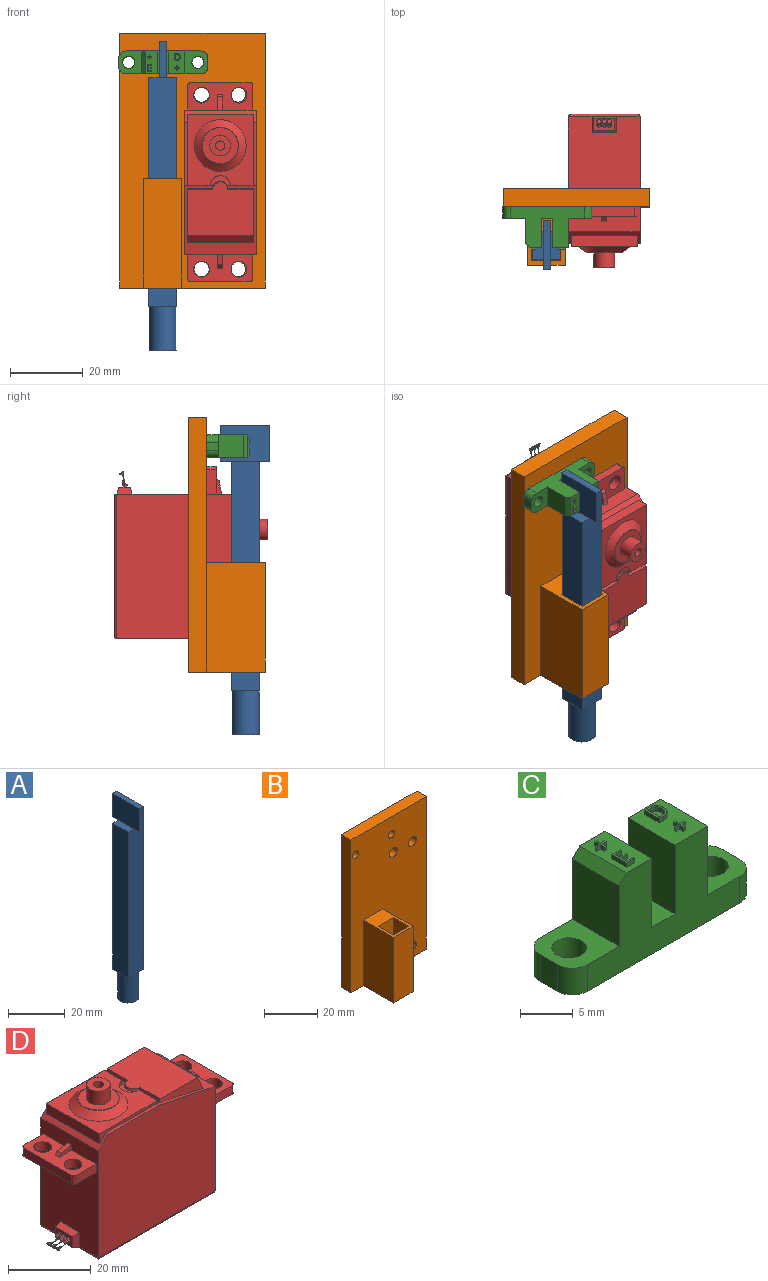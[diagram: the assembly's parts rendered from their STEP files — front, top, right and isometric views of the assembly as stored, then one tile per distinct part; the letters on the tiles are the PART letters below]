
ASSEMBLY  parts=4 mates=4
PART A: 16 faces, bbox 7.7x13.5x85 mm
  f0: plane 63x7.7mm, normal (0,1,0), area 485.1mm2, adj f1,f3,f4,f5,f12,f13
  f1: plane 63x7.7mm, normal (-1,0,0), area 485.1mm2, adj f0,f2,f5,f13
  f2: plane 63x7.7mm, normal (0,-1,0), area 485.1mm2, adj f1,f3,f4,f5,f6,f13
  f3: plane 63x7.7mm, normal (1,0,0), area 485.1mm2, adj f0,f2,f4,f13
  f4: plane 7.7x2.85mm, normal (0,0,1), area 21.9mm2, adj f0,f2,f3,f10
  f5: plane 7.7x2.85mm, normal (0,0,1), area 21.9mm2, adj f0,f1,f2,f8
  f6: plane 2.81x2mm, normal (0,0,-1), area 5.6mm2, adj f2,f8,f9,f10
  f7: plane 10x2mm, normal (0,1,0), area 20mm2, adj f8,f10,f11,f12
  f8: plane 13.51x10mm, normal (-1,0,0), area 135.1mm2, adj f5,f6,f7,f9,f11,f12
  f9: plane 10x2mm, normal (0,-1,0), area 20mm2, adj f6,f8,f10,f11
  f10: plane 13.51x10mm, normal (1,0,0), area 135.1mm2, adj f4,f6,f7,f9,f11,f12
  f11: plane 13.51x2mm, normal (0,0,1), area 27mm2, adj f7,f8,f9,f10
  f12: plane 3x2mm, normal (0,0,-1), area 6mm2, adj f0,f7,f8,f10
  f13: plane 7.7x7.7mm, normal (0,0,-1), area 15.1mm2, adj f0,f1,f2,f3,f14
  f14: cylinder r=3.75mm len=12mm, axis (0,0,-1), area 282.7mm2, adj f13,f15
  f15: plane 7.5x7.5mm, normal (0,0,-1), area 44.2mm2, adj f14
PART B: 20 faces, bbox 40x21x70 mm
  f0: plane 40x5mm, normal (0,0,1), area 200mm2, adj f1,f3,f4,f5
  f1: plane 70x5mm, normal (-1,0,0), area 350mm2, adj f0,f2,f4,f5
  f2: plane 40x21mm, normal (0,0,-1), area 302.4mm2, adj f1,f3,f4,f5,f6,f7,f8,f9
  f3: plane 70x5mm, normal (1,0,0), area 350mm2, adj f0,f2,f4,f5
  f4: plane 70x40mm, normal (0,-1,0), area 2415.5mm2, adj f0,f1,f2,f3,f6,f12,f13,f14
  f5: plane 70x40mm, normal (0,1,0), area 2727.5mm2, adj f0,f1,f2,f3,f14,f15,f16,f17
  f6: plane 30x16mm, normal (-1,0,0), area 480mm2, adj f2,f4,f7,f13
  f7: plane 30x10.4mm, normal (0,-1,0), area 312mm2, adj f2,f6,f12,f13
  f8: plane 30x8mm, normal (1,0,0), area 240mm2, adj f2,f9,f11,f13
  f9: plane 30x8mm, normal (0,-1,0), area 240mm2, adj f2,f8,f10,f13
  f10: plane 30x8mm, normal (-1,0,0), area 240mm2, adj f2,f9,f11,f13
  f11: plane 30x8mm, normal (0,1,0), area 240mm2, adj f2,f8,f10,f13
  f12: plane 30x16mm, normal (1,0,0), area 480mm2, adj f2,f4,f7,f13
  f13: plane 16x10.4mm, normal (0,0,1), area 102.4mm2, adj f4,f6,f7,f8,f9,f10,f11,f12
  f14: cylinder r=2.1mm len=5mm, axis (0,-1,0), area 66mm2, adj f4,f5
  f15: cylinder r=2.1mm len=5mm, axis (0,-1,0), area 66mm2, adj f4,f5
  f16: cylinder r=2.1mm len=5mm, axis (0,-1,0), area 66mm2, adj f4,f5
  f17: cylinder r=2.1mm len=5mm, axis (0,-1,0), area 66mm2, adj f4,f5
  f18: cylinder r=1.65mm len=5mm, axis (0,-1,0), area 51.8mm2, adj f4,f5
  f19: cylinder r=1.65mm len=5mm, axis (0,-1,0), area 51.8mm2, adj f4,f5
PART C: 76 faces, bbox 24.5x6.3x11.6 mm
  f0: plane 6.3x4.4mm, normal (0,0,1), area 24.5mm2, adj f2,f3,f9,f11,f53,f54,f55,f56
  f1: plane 6.3x3.4mm, normal (0,0,1), area 20mm2, adj f2,f3,f7,f14,f21,f22,f23,f24
  f2: plane 20.5x11.1mm, normal (0,1,0), area 133.5mm2, adj f0,f1,f6,f7,f8,f9,f10,f11
  f3: plane 20.5x11.1mm, normal (0,-1,0), area 133.5mm2, adj f0,f1,f6,f7,f8,f9,f10,f11
  f4: plane 3.1x2.3mm, normal (-1,0,0), area 7.1mm2, adj f6,f12,f17,f18
  f5: plane 3.1x2.3mm, normal (1,0,0), area 7.1mm2, adj f6,f10,f19,f20
  f6: plane 24.5x6.3mm, normal (0,0,-1), area 133.8mm2, adj f2,f3,f4,f5,f15,f16,f17,f18
  f7: plane 8x6.3mm, normal (1,0,0), area 50.4mm2, adj f1,f2,f3,f8
  f8: plane 6.3x3.1mm, normal (0,0,1), area 19.5mm2, adj f2,f3,f7,f9
  f9: plane 8x6.3mm, normal (-1,0,0), area 50.4mm2, adj f0,f2,f3,f8
  f10: plane 6.3x6.3mm, normal (0,0,1), area 29.4mm2, adj f2,f3,f5,f11,f16,f19,f20
  f11: plane 8x6.3mm, normal (1,0,0), area 50.4mm2, adj f0,f2,f3,f10
  f12: plane 6.3x6.3mm, normal (0,0,1), area 29.4mm2, adj f2,f3,f4,f13,f15,f17,f18
  f13: plane 7x6.3mm, normal (-1,0,0), area 44.1mm2, adj f2,f3,f12,f14
  f14: plane 6.3x1mm, normal (-0.71,0,0.71), area 8.9mm2, adj f1,f2,f3,f13
  f15: cylinder r=1.65mm len=3.3mm, axis (0,0,-1), area 32.1mm2, adj f6,f12
  f16: cylinder r=1.65mm len=3.3mm, axis (0,0,-1), area 32.1mm2, adj f6,f10
  f17: cylinder r=2mm len=3.1mm, axis (0,0,1), area 9.7mm2, adj f2,f4,f6,f12
  f18: cylinder r=2mm len=3.1mm, axis (0,0,-1), area 9.7mm2, adj f3,f4,f6,f12
  f19: cylinder r=2mm len=3.1mm, axis (0,0,1), area 9.7mm2, adj f3,f5,f6,f10
  f20: cylinder r=2mm len=3.1mm, axis (0,0,-1), area 9.7mm2, adj f2,f5,f6,f10
  f21: plane 0.56x0.5mm, normal (0,1,0), area 0.3mm2, adj f1,f22,f32,f33
  f22: plane 0.58x0.5mm, normal (1,0,0), area 0.3mm2, adj f1,f21,f23,f33
  f23: plane 0.5x0.19mm, normal (0,1,0), area 0.1mm2, adj f1,f22,f24,f33
  f24: plane 0.58x0.5mm, normal (-1,0,0), area 0.3mm2, adj f1,f23,f25,f33
  f25: plane 0.56x0.5mm, normal (0,1,0), area 0.3mm2, adj f1,f24,f26,f33
  f26: plane 0.5x0.19mm, normal (-1,0,0), area 0.1mm2, adj f1,f25,f27,f33
  f27: plane 0.56x0.5mm, normal (0,-1,0), area 0.3mm2, adj f1,f26,f28,f33
  f28: plane 0.58x0.5mm, normal (-1,0,0), area 0.3mm2, adj f1,f27,f29,f33
  f29: plane 0.5x0.19mm, normal (0,-1,0), area 0.1mm2, adj f1,f28,f30,f33
  f30: plane 0.58x0.5mm, normal (1,0,0), area 0.3mm2, adj f1,f29,f31,f33
  f31: plane 0.56x0.5mm, normal (0,-1,0), area 0.3mm2, adj f1,f30,f32,f33
  f32: plane 0.5x0.19mm, normal (1,0,0), area 0.1mm2, adj f1,f21,f31,f33
  f33: plane 1.35x1.3mm, normal (0,0,1), area 0.5mm2, adj f21,f22,f23,f24,f25,f26,f27,f28
  f34: plane 1.11x0.5mm, normal (0,-1,0), area 0.6mm2, adj f1,f35,f45,f46
  f35: plane 0.5x0.21mm, normal (1,0,0), area 0.1mm2, adj f1,f34,f36,f46
  f36: plane 0.88x0.5mm, normal (0,1,0), area 0.4mm2, adj f1,f35,f37,f46
  f37: plane 0.73x0.5mm, normal (1,0,0), area 0.4mm2, adj f1,f36,f38,f46
  f38: plane 0.82x0.5mm, normal (0,-1,0), area 0.4mm2, adj f1,f37,f39,f46
  f39: plane 0.5x0.2mm, normal (1,0,0), area 0.1mm2, adj f1,f38,f40,f46
  f40: plane 0.82x0.5mm, normal (0,1,0), area 0.4mm2, adj f1,f39,f41,f46
  f41: plane 0.64x0.5mm, normal (1,0,0), area 0.3mm2, adj f1,f40,f42,f46
  f42: plane 0.88x0.5mm, normal (0,-1,0), area 0.4mm2, adj f1,f41,f43,f46
  f43: plane 0.5x0.21mm, normal (1,0,0), area 0.1mm2, adj f1,f42,f44,f46
  f44: plane 1.11x0.5mm, normal (0,1,0), area 0.6mm2, adj f1,f43,f45,f46
  f45: plane 1.98x0.5mm, normal (-1,0,0), area 1mm2, adj f1,f34,f44,f46
  f46: plane 1.98x1.11mm, normal (0,0,1), area 1mm2, adj f34,f35,f36,f37,f38,f39,f40,f41
  f47: extruded ~0.58x0.5mm, area 0.3mm2, adj f48,f60,f61,f62
  f48: extruded ~0.6x0.5mm, area 0.3mm2, adj f47,f49,f61,f62
  f49: extruded ~0.62x0.5mm, area 0.3mm2, adj f48,f50,f61,f62
  f50: plane 0.5x0.28mm, normal (0,1,0), area 0.1mm2, adj f49,f51,f61,f62
  f51: plane 1.58x0.5mm, normal (1,0,0), area 0.8mm2, adj f50,f52,f61,f62
  f52: plane 0.5x0.34mm, normal (0,-1,0), area 0.2mm2, adj f51,f60,f61,f62
  f53: extruded ~0.75x0.5mm, area 0.4mm2, adj f0,f54,f59,f61
  f54: extruded ~0.72x0.5mm, area 0.4mm2, adj f0,f53,f55,f61
  f55: extruded ~0.72x0.5mm, area 0.4mm2, adj f0,f54,f56,f61
  f56: plane 0.61x0.5mm, normal (0,1,0), area 0.3mm2, adj f0,f55,f57,f61
  f57: plane 1.98x0.5mm, normal (-1,0,0), area 1mm2, adj f0,f56,f58,f61
  f58: plane 0.55x0.5mm, normal (0,-1,0), area 0.3mm2, adj f0,f57,f59,f61
  f59: extruded ~0.77x0.5mm, area 0.4mm2, adj f0,f53,f58,f61
  f60: extruded ~0.58x0.5mm, area 0.3mm2, adj f47,f52,f61,f62
  f61: plane 1.98x1.58mm, normal (0,0,1), area 1.2mm2, adj f47,f48,f49,f50,f51,f52,f53,f54
  f62: plane 1.58x1.11mm, normal (0,0,1), area 1.5mm2, adj f47,f48,f49,f50,f51,f52,f60
  f63: plane 0.56x0.5mm, normal (0,1,0), area 0.3mm2, adj f0,f64,f74,f75
  f64: plane 0.58x0.5mm, normal (1,0,0), area 0.3mm2, adj f0,f63,f65,f75
  f65: plane 0.5x0.19mm, normal (0,1,0), area 0.1mm2, adj f0,f64,f66,f75
  f66: plane 0.58x0.5mm, normal (-1,0,0), area 0.3mm2, adj f0,f65,f67,f75
  f67: plane 0.56x0.5mm, normal (0,1,0), area 0.3mm2, adj f0,f66,f68,f75
  f68: plane 0.5x0.19mm, normal (-1,0,0), area 0.1mm2, adj f0,f67,f69,f75
  f69: plane 0.56x0.5mm, normal (0,-1,0), area 0.3mm2, adj f0,f68,f70,f75
  f70: plane 0.58x0.5mm, normal (-1,0,0), area 0.3mm2, adj f0,f69,f71,f75
  f71: plane 0.5x0.19mm, normal (0,-1,0), area 0.1mm2, adj f0,f70,f72,f75
  f72: plane 0.58x0.5mm, normal (1,0,0), area 0.3mm2, adj f0,f71,f73,f75
  f73: plane 0.56x0.5mm, normal (0,-1,0), area 0.3mm2, adj f0,f72,f74,f75
  f74: plane 0.5x0.19mm, normal (1,0,0), area 0.1mm2, adj f0,f63,f73,f75
  f75: plane 1.35x1.3mm, normal (0,0,1), area 0.5mm2, adj f63,f64,f65,f66,f67,f68,f69,f70
PART D: 74 faces, bbox 57.3x22.3x44.8 mm
  f0: plane 5.72x3.18mm, normal (-1,0,0), area 14.3mm2, adj f64,f65,f66,f67,f68,f70,f72
  f1: plane 31.5x19.69mm, normal (-1,0,0), area 544.1mm2, adj f9,f12,f13,f14,f23,f24,f25,f26
  f2: plane 9.91x9.91mm, normal (0,0,1), area 51.4mm2, adj f57,f61
  f3: plane 11.76x11.76mm, normal (0,0,1), area 2mm2, adj f56,f57
  f4: plane 22.27x20.55mm, normal (0,0,1), area 182.3mm2, adj f32,f33,f34,f35,f36,f37,f56
  f5: plane 19.8x19.16mm, normal (0.2,0,0.98), area 103.5mm2, adj f6,f7,f8,f10,f12,f13,f32,f33
  f6: plane 17.34x0.89mm, normal (0,0,1), area 15.4mm2, adj f5,f9,f12,f35
  f7: plane 5.58x2.6mm, normal (0,0,1), area 11.2mm2, adj f5,f34,f39
  f8: plane 17.34x0.84mm, normal (0,0,1), area 14.5mm2, adj f5,f9,f13,f36
  f9: plane 19.69x3.3mm, normal (-0.71,0,0.71), area 37.1mm2, adj f1,f6,f8,f12,f13,f35,f36,f37
  f10: plane 30.83x19.69mm, normal (1,0,0), area 558.8mm2, adj f5,f12,f13,f17,f18,f19,f20,f21
  f11: plane 38.16x18.16mm, normal (0,0,-1), area 693.1mm2, adj f14,f15,f16,f17
  f12: plane 39.69x34.8mm, normal (0,-1,0), area 1337.8mm2, adj f1,f5,f6,f9,f10,f15
  f13: plane 39.69x34.8mm, normal (0,1,0), area 1337.8mm2, adj f1,f5,f8,f9,f10,f16
  f14: cylinder r=0.76mm len=19.69mm, axis (0,1,0), area 22.6mm2, adj f1,f11,f15,f16,f66
  f15: cylinder r=0.76mm len=39.69mm, axis (1,0,0), area 46.6mm2, adj f11,f12,f14,f17
  f16: cylinder r=0.76mm len=39.69mm, axis (-1,0,0), area 46.6mm2, adj f11,f13,f14,f17
  f17: cylinder r=0.76mm len=19.69mm, axis (0,1,0), area 22.6mm2, adj f10,f11,f15,f16
  f18: plane 6.73x2.54mm, normal (0,-1,0), area 17.1mm2, adj f10,f19,f21,f29
  f19: plane 17.91x7.49mm, normal (0,0,-1), area 104.6mm2, adj f10,f18,f20,f22,f28,f29,f46,f47
  f20: plane 6.73x2.54mm, normal (0,1,0), area 17.1mm2, adj f10,f19,f21,f28
  f21: plane 17.91x7.49mm, normal (0,0,1), area 99.1mm2, adj f10,f18,f20,f22,f28,f29,f46,f47
  f22: plane 16.38x2.54mm, normal (1,0,0), area 41.6mm2, adj f19,f21,f28,f29
  f23: plane 6.73x2.54mm, normal (0,1,0), area 17.1mm2, adj f1,f24,f26,f30
  f24: plane 17.91x7.49mm, normal (0,0,-1), area 104.6mm2, adj f1,f23,f25,f27,f30,f31,f58,f59
  f25: plane 6.73x2.54mm, normal (0,-1,0), area 17.1mm2, adj f1,f24,f26,f31
  f26: plane 17.91x7.49mm, normal (0,0,1), area 98.6mm2, adj f1,f23,f25,f27,f30,f31,f52,f54
  f27: plane 16.38x2.54mm, normal (-1,0,0), area 41.6mm2, adj f24,f26,f30,f31
  f28: cylinder r=0.76mm len=2.54mm, axis (0,0,1), area 3mm2, adj f19,f20,f21,f22
  f29: cylinder r=0.76mm len=2.54mm, axis (0,0,-1), area 3mm2, adj f18,f19,f21,f22
  f30: cylinder r=0.76mm len=2.54mm, axis (0,0,-1), area 3mm2, adj f23,f24,f26,f27
  f31: cylinder r=0.76mm len=2.54mm, axis (0,0,1), area 3mm2, adj f24,f25,f26,f27
  f32: plane 6.19x0.83mm, normal (1,0,0), area 5.2mm2, adj f4,f5,f34,f35
  f33: plane 6.19x0.83mm, normal (1,0,0), area 5.2mm2, adj f4,f5,f34,f36
  f34: cylinder r=2.79mm len=5.59mm, axis (0,0,-1), area 7mm2, adj f4,f5,f7,f32,f33
  f35: plane 19.69x2.95mm, normal (0,-1,0), area 18mm2, adj f4,f5,f6,f9,f32,f37
  f36: plane 19.69x2.95mm, normal (0,1,0), area 18mm2, adj f4,f5,f8,f9,f33,f37
  f37: plane 17.96x2.95mm, normal (-1,0,0), area 53mm2, adj f4,f9,f35,f36
  f38: plane 18.55x15.39mm, normal (0,0,1), area 235mm2, adj f40,f41,f42,f43,f44,f45
  f39: plane 3.79x1.2mm, normal (-0.2,0,-0.98), area 2.7mm2, adj f7,f43
  f40: plane 14.82x4.09mm, normal (0,1,0), area 33.7mm2, adj f5,f38,f41,f42
  f41: plane 18.04x4.09mm, normal (0.91,0,0.42), area 81.2mm2, adj f5,f38,f40,f45
  f42: plane 6.94x1mm, normal (-0.98,0,0.2), area 7.1mm2, adj f5,f38,f40,f43
  f43: bspline ~4.28x4.22mm, area 4.9mm2, adj f5,f38,f39,f42,f44
  f44: plane 6.97x1mm, normal (-0.98,0,0.2), area 7.1mm2, adj f5,f38,f43,f45
  f45: bspline ~14.82x4.09mm, area 33.7mm2, adj f5,f38,f41,f44
  f46: cylinder r=2.16mm len=4.32mm, axis (0,0,1), area 34.5mm2, adj f19,f21
  f47: cylinder r=2.16mm len=4.32mm, axis (0,0,1), area 34.5mm2, adj f19,f21
  f48: plane 1.4x1.19mm, normal (0.75,0,0.67), area 2.2mm2, adj f21,f49,f50,f51
  f49: plane 2.87x1.4mm, normal (0.23,0,0.97), area 4.1mm2, adj f10,f48,f50,f51
  f50: plane 3.93x1.88mm, normal (0,-1,0), area 5mm2, adj f10,f21,f48,f49
  f51: plane 3.93x1.88mm, normal (0,1,0), area 5mm2, adj f10,f21,f48,f49
  f52: plane 1.4x0.84mm, normal (-0.76,0,0.65), area 1.5mm2, adj f26,f53,f54,f55
  f53: plane 3.58x1.4mm, normal (-0.19,0,0.98), area 5.1mm2, adj f1,f52,f54,f55
  f54: plane 4.3x1.55mm, normal (0,-1,0), area 4.6mm2, adj f1,f26,f52,f53
  f55: plane 4.3x1.55mm, normal (0,1,0), area 4.6mm2, adj f1,f26,f52,f53
  f56: bspline ~14.18x14.1mm, area 101.7mm2, adj f3,f4
  f57: cylinder r=4.95mm len=9.91mm, axis (0,0,-1), area 4mm2, adj f2,f3
  f58: cylinder r=2.16mm len=4.32mm, axis (0,0,1), area 34.5mm2, adj f24,f26
  f59: cylinder r=2.16mm len=4.32mm, axis (0,0,1), area 34.5mm2, adj f24,f26
  f60: plane 5.72x5.72mm, normal (0,0,1), area 20.6mm2, adj f61,f62
  f61: cylinder r=2.86mm len=5.72mm, axis (0,0,-1), area 73mm2, adj f2,f60
  f62: cylinder r=1.27mm len=4.06mm, axis (0,0,-1), area 32.4mm2, adj f60,f63
  f63: plane 2.54x2.54mm, normal (0,0,1), area 5.1mm2, adj f62
  f64: plane 4.19x1.91mm, normal (-0.26,0.97,0), area 7.3mm2, adj f0,f1,f65,f66
  f65: plane 6.73x1.91mm, normal (-0.26,0,0.97), area 12.3mm2, adj f0,f1,f64,f67
  f66: plane 6.73x1.91mm, normal (-0.26,0,-0.97), area 12.3mm2, adj f0,f14,f64,f67
  f67: plane 4.19x1.91mm, normal (-0.26,-0.97,0), area 7.3mm2, adj f0,f1,f65,f66
  f68: revolved ~4.22x2.14mm, area 16.1mm2, adj f0,f69
  f69: plane 1.27x1.05mm, normal (-0.82,0,-0.57), area 1.3mm2, adj f68
  f70: revolved ~4.22x2.14mm, area 16.1mm2, adj f0,f71
  f71: plane 1.27x1.05mm, normal (-0.82,0,-0.57), area 1.3mm2, adj f70
  f72: revolved ~4.22x2.14mm, area 16.1mm2, adj f0,f73
  f73: plane 1.27x1.05mm, normal (-0.82,0,-0.57), area 1.3mm2, adj f72
PLACE A t=(36.07,3.82,81.39)mm
PLACE B t=(35.87,3.62,58.7)mm
PLACE C rot(axis=(1,0,0),90deg) t=(27.87,-1.38,90.7)mm
PLACE D rot(axis=(0.58,0.58,-0.58),120deg) t=(53.35,24.12,77.63)mm
MATE fastened D.f46 <-> B.f15  axis (0,1,0) through (38.37,-1.38,33.88)mm
MATE planar B.f9 <-> A.f0  axis (0,-1,0) through (27.57,-8.18,43.7)mm
MATE planar B.f10 <-> A.f3  axis (-1,0,0) through (31.57,-12.18,43.7)mm
MATE fastened B.f19 <-> C.f15  axis (0,-1,0) through (18.37,-1.38,90.7)mm
